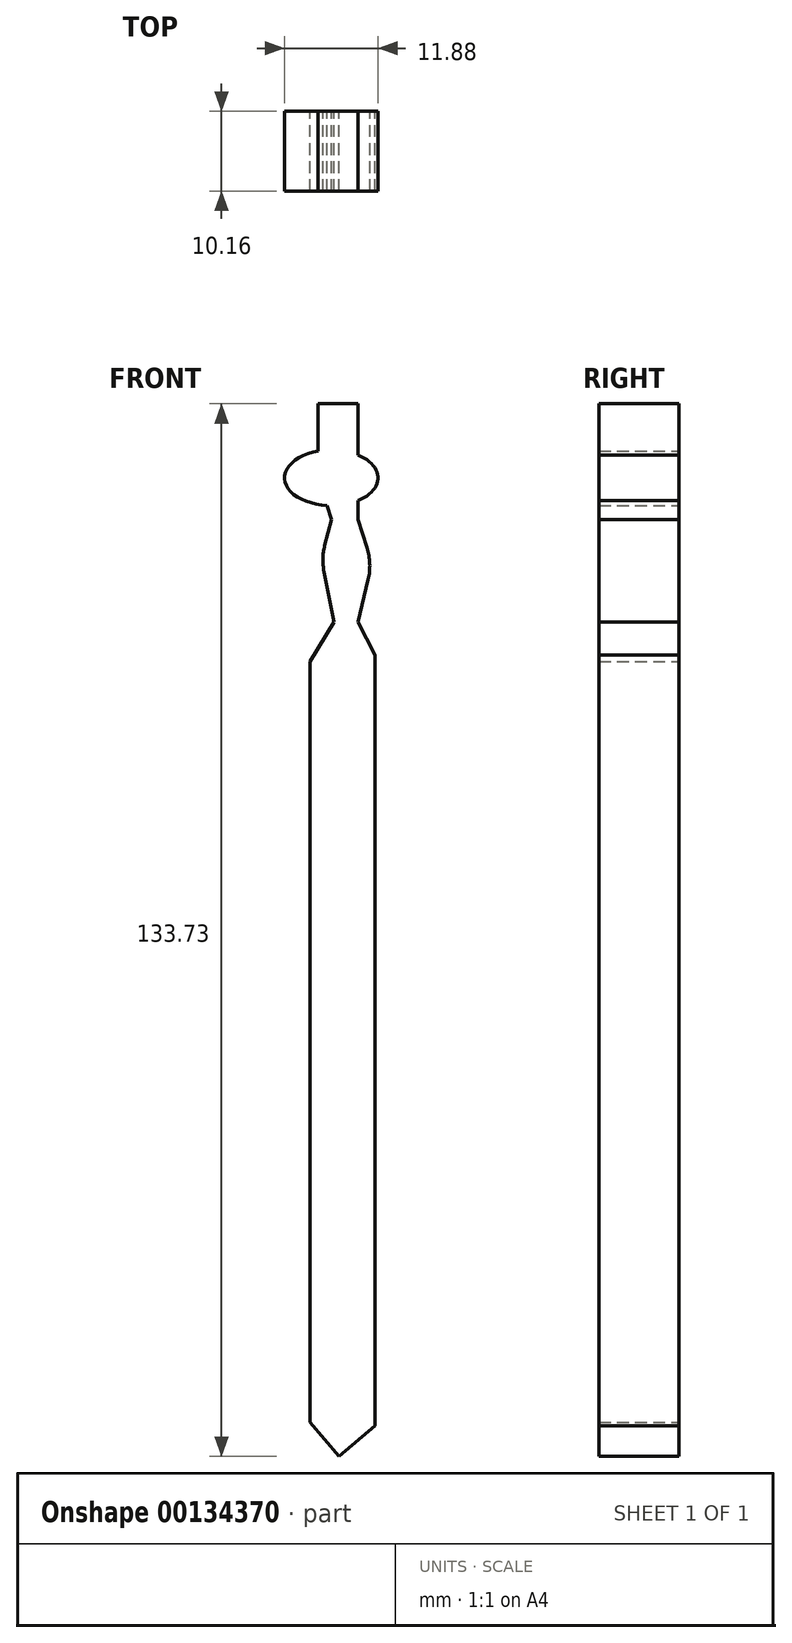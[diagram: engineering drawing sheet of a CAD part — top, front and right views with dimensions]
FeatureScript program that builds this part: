
annotation { "Feature Type Name" : "Feature", "Feature Type Description" : "" }
export const myFeature = defineFeature(function(context is Context, id is Id, definition is map)
    precondition{}
    {
        {
            var Q0;
            Q0=qCreatedBy(makeId("Front.planeOp"),FACE);
            var sketch = newSketch(context, id + "F0", { "sketchPlane" : qUnion([Q0])});
            skLineSegment(sketch, "E0", {"start": v(-5.07, 50.4) * mm, "end": v(-5.07, 57.24) * mm});
            skLineSegment(sketch, "E1", {"start": v(0, 57.24) * mm, "end": v(0, 50.32) * mm});
            skLineSegment(sketch, "E2", {"start": v(0, 50.32) * mm, "end": v(-3.4, 50.32) * mm});
            skLineSegment(sketch, "E3", {"start": v(-3.4, 50.32) * mm, "end": v(-5.07, 50.4) * mm});
            skLineSegment(sketch, "E4", {"start": v(-5.07, 50.4) * mm, "end": v(-3.4, 45.03) * mm});
            skPoint(sketch, "E4.endSnap0", {"position": v(-3.4, 47.3) * mm});
            skLineSegment(sketch, "E5", {"start": v(-3.4, 45.03) * mm, "end": v(-4.66, 40.06) * mm});
            skLineSegment(sketch, "E6", {"start": v(0, 50.32) * mm, "end": v(0, 45.03) * mm});
            skLineSegment(sketch, "E7", {"start": v(0, 45.03) * mm, "end": v(1.76, 39.44) * mm});
            skLineSegment(sketch, "E8", {"start": v(1.76, 39.44) * mm, "end": v(0, 31.98) * mm});
            skLineSegment(sketch, "E9", {"start": v(0, 31.98) * mm, "end": v(-3.07, 31.98) * mm});
            skLineSegment(sketch, "E10", {"start": v(-3.07, 31.98) * mm, "end": v(-6.1, 27.02) * mm});
            skLineSegment(sketch, "E11", {"start": v(-6.1, 27.02) * mm, "end": v(-6.1, -69.66) * mm});
            skLineSegment(sketch, "E12", {"start": v(-6.1, -69.66) * mm, "end": v(-2.43, -73.99) * mm});
            skLineSegment(sketch, "E13", {"start": v(-2.43, -73.99) * mm, "end": v(2.17, -70.07) * mm});
            skLineSegment(sketch, "E14", {"start": v(2.17, -70.07) * mm, "end": v(2.17, 27.78) * mm});
            skLineSegment(sketch, "E15", {"start": v(2.17, 27.78) * mm, "end": v(0, 31.98) * mm});
            skLineSegment(sketch, "E16", {"start": v(-4.66, 40.06) * mm, "end": v(-3.07, 31.98) * mm});
            skEllipse(sketch, "E17", {"center": v(-3.4, 50.32) * mm, "majorRadius": 5.94 * mm, "minorRadius": 3.53 * mm, "majorAxis": v(1, 0)});
            skLineSegment(sketch, "E18", {"start": v(-5.07, 57.24) * mm, "end": v(-5.07, 59.74) * mm});
            skLineSegment(sketch, "E19", {"start": v(-5.07, 59.74) * mm, "end": v(0, 59.74) * mm});
            skLineSegment(sketch, "E20", {"start": v(0, 59.74) * mm, "end": v(0, 57.24) * mm});
            skSolve(sketch);
        }
        {
            var Q0;
            Q0 = qSketchRegion(id + "F0", true);
            extrude(context, id + "F1", {"entities" : qUnion([Q0]), "depth" : 10.16 * mm});
        }
        {
            var Q0;
            Q0=makeQuery(id+"F1.opExtrude","SWEPT_EDGE",EDGE,{"disambiguationData":[OSD([sQuery(id+"F0.wireOp",EDGE,"E5"),sQuery(id+"F0.wireOp",EDGE,"E16")])]});
            var Q1;
            Q1=makeQuery(id+"F1.opExtrude","SWEPT_EDGE",EDGE,{"disambiguationData":[OSD([sQuery(id+"F0.wireOp",EDGE,"E7"),sQuery(id+"F0.wireOp",EDGE,"E8")])]});
            fillet(context, id + "F2", {"entities" : qUnion([Q0, Q1]), "radius" : 7.62 * mm, "tangentPropagation" : true, "allowEdgeOverflow" : false});
        }
    });
